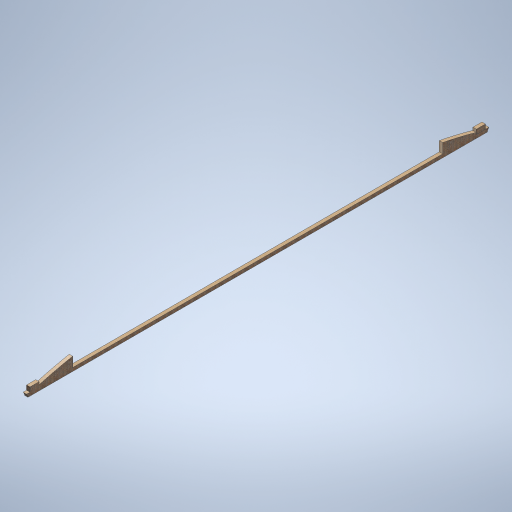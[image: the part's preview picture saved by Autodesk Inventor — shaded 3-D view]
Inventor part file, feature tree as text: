
AUTODESK INVENTOR PART (.ipt)
format: ipt  version: 2024.2 (Build 282272000, 272)  size: 354,816 bytes
history: native  units: mm
features: sketch x9, extrude x5
ambient origin geometry x8: Origin, YZ Plane, XZ Plane, XY Plane, X Axis, Y Axis, Z Axis, Center Point
bodies: Solid1 (feature_tree)
feature tree (14):
  sketch  "Sketch1"  dims[d0=300.0mm d1=300.0mm]
  extrude  "Extrusion1"  Depth=300.0mm
  sketch  "Sketch4"  dims[d11=250.0mm d12=60.0deg]
  sketch  "Sketch5"  dims[d13=25.307274mm d14=300.0mm d15=0.0mm]
  extrude  "Extrusion3"  Depth=1000.0mm
  sketch  "Sketch7"  dims[d18=304.0mm]
  extrude  "Extrusion4"  TaperAngle=60.0deg  [1 undecoded]
  extrude  "Extrusion5"  Depth=300.0mm TaperAngle=0.0deg
  extrude  "Extrusion6"  Depth=799.0mm
  sketch  "Sketch2"  dims[d2=38608.0mm d3=0.0mm d10=1000.0mm]
  sketch  "Sketch6"  dims[d16=304.0mm d17=799.0mm]
  sketch  "Sketch8"  dims[d19=799.0mm]
  sketch  "Sketch9"  dims[d20=90.0deg]
  sketch  "Sketch11"  dims[d21=400.0mm d22=0.0mm d23=300.0mm d24=0.0mm d25=2950.0mm d27=160.0mm d28=863.0mm d29=90.0deg d30=35000.0mm d31=300.0mm d32=0.0mm d4=500.0mm d5=0.872665mm d33=500.0mm d34=0.872665mm]
note: 1 required parameter value undecoded (feature->parameter linkage not recoverable at this tier; creation-order binding heuristic only, values carry confidence <= 0.55)
